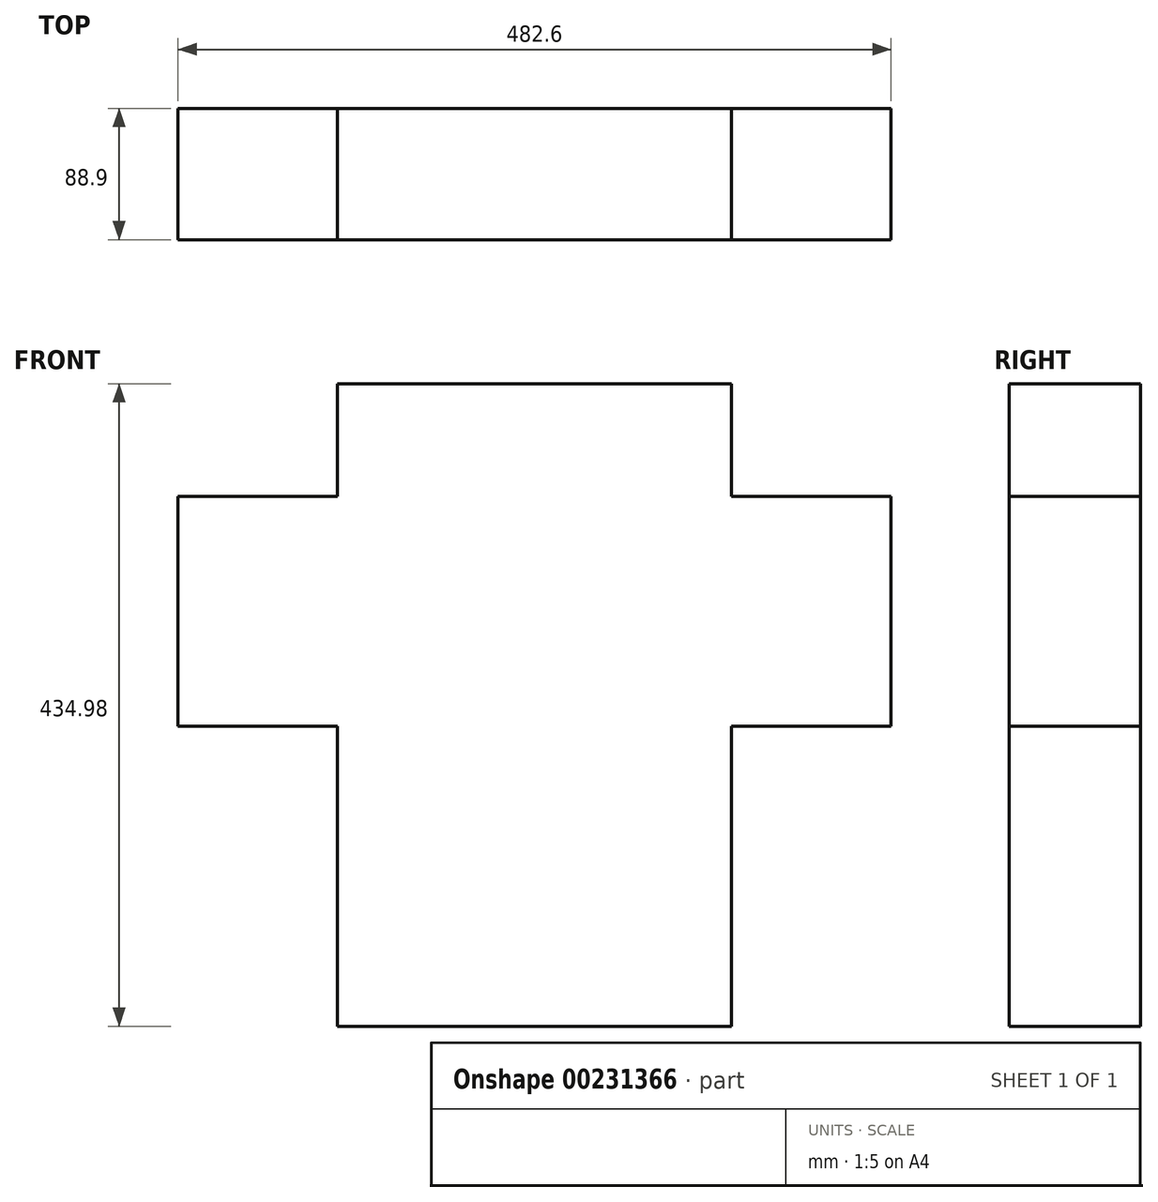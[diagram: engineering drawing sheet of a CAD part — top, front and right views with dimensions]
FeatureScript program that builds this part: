
annotation { "Feature Type Name" : "Feature", "Feature Type Description" : "" }
export const myFeature = defineFeature(function(context is Context, id is Id, definition is map)
    precondition{}
    {
        {
            var Q0;
            Q0=qCreatedBy(makeId("Front.planeOp"),FACE);
            var sketch = newSketch(context, id + "F0", { "sketchPlane" : qUnion([Q0])});
            skLineSegment(sketch, "E0", {"start": v(-266.11, 231.78) * mm, "end": v(-266.11, 155.58) * mm});
            skLineSegment(sketch, "E1", {"start": v(-266.11, 155.58) * mm, "end": v(-374.06, 155.57) * mm});
            skLineSegment(sketch, "E2", {"start": v(-374.06, 155.57) * mm, "end": v(-374.06, 0) * mm});
            skLineSegment(sketch, "E3", {"start": v(-374.06, 0) * mm, "end": v(-266.11, 0) * mm});
            skLineSegment(sketch, "E4", {"start": v(-266.11, 0) * mm, "end": v(-266.11, -203.2) * mm});
            skLineSegment(sketch, "E5", {"start": v(-266.11, -203.2) * mm, "end": v(0.59, -203.2) * mm});
            skLineSegment(sketch, "E6", {"start": v(0.59, -203.2) * mm, "end": v(0.59, 0) * mm});
            skLineSegment(sketch, "E7", {"start": v(0.59, 0) * mm, "end": v(108.54, 0) * mm});
            skLineSegment(sketch, "E8", {"start": v(108.54, 0) * mm, "end": v(108.54, 155.58) * mm});
            skLineSegment(sketch, "E9", {"start": v(108.54, 155.58) * mm, "end": v(0.59, 155.57) * mm});
            skLineSegment(sketch, "E10", {"start": v(0.59, 155.57) * mm, "end": v(0.59, 231.78) * mm});
            skLineSegment(sketch, "E11", {"start": v(0.59, 231.78) * mm, "end": v(-266.11, 231.78) * mm});
            skSolve(sketch);
        }
        {
            var Q0;
            Q0=makeQuery(id+"F0.imprint","IMPRINT",FACE,{"disambiguationData":[TD([[makeQuery(id+"F0.imprint","IMPRINT",EDGE,{"derivedFrom":sQuery(id+"F0.wireOp",EDGE,"E0")}),1.0]])]});
            extrude(context, id + "F1", {"entities" : qUnion([Q0]), "depth" : 88.9 * mm});
        }
    });
